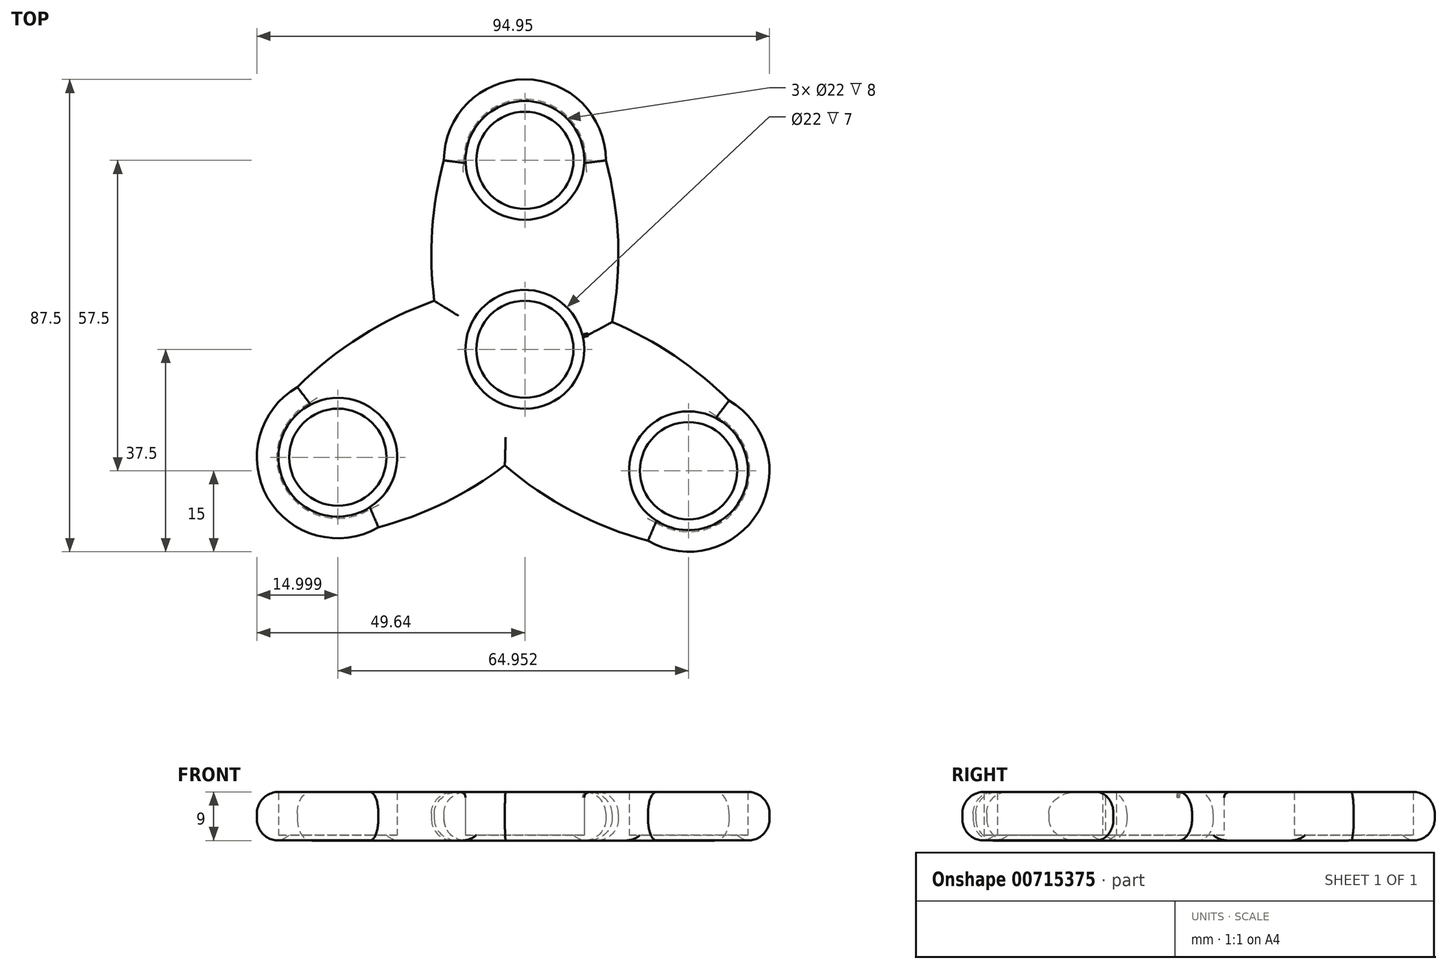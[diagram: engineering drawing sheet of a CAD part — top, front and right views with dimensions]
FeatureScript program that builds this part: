
annotation { "Feature Type Name" : "Feature", "Feature Type Description" : "" }
export const myFeature = defineFeature(function(context is Context, id is Id, definition is map)
    precondition{}
    {
        {
            var Q0;
            Q0=qCreatedBy(makeId("Top.planeOp"),FACE);
            var sketch = newSketch(context, id + "F0", { "sketchPlane" : qUnion([Q0])});
            skCircle(sketch, "E0", {"center": v(0, 0) * mm, "radius": 11 * mm});
            skPoint(sketch, "E1", {"position": v(11, 0) * mm});
            skPoint(sketch, "E2", {"position": v(-11, 0) * mm});
            skLineSegment(sketch, "E3", {"start": v(0, 0) * mm, "end": v(0, 35) * mm});
            skCircle(sketch, "E4", {"center": v(0, 0) * mm, "radius": 15 * mm});
            skCircle(sketch, "E5", {"center": v(0, 35) * mm, "radius": 11 * mm});
            skPoint(sketch, "E6", {"position": v(0, 46) * mm});
            skPoint(sketch, "E7", {"position": v(0, 24) * mm});
            skCircle(sketch, "E8", {"center": v(0, 35) * mm, "radius": 15 * mm});
            skArc(sketch, "E9", {"start": v(-15, 35) * mm, "mid": v(-17.31, 17.5) * mm, "end": v(-15, 0) * mm});
            skPoint(sketch, "E10.endSnap0", {"position": v(-17.31, 17.5) * mm});
            skPoint(sketch, "E11.MirrorP", {"position": v(17.31, 17.5) * mm});
            skArc(sketch, "E12.MirrorCS", {"start": v(15, 35) * mm, "mid": v(17.31, 17.5) * mm, "end": v(15, 0) * mm});
            skPoint(sketch, "E13.1.0", {"position": v(-10.83, -26.24) * mm});
            skCircle(sketch, "E13.1.1", {"center": v(-34.64, -20) * mm, "radius": 11 * mm});
            skPoint(sketch, "E13.1.2", {"position": v(-44.17, -25.5) * mm});
            skPoint(sketch, "E13.1.3", {"position": v(-25.11, -14.5) * mm});
            skPoint(sketch, "E13.1.4", {"position": v(-34.64, -20) * mm});
            skCircle(sketch, "E13.1.5", {"center": v(-34.64, -20) * mm, "radius": 15 * mm});
            skPoint(sketch, "E13.1.6", {"position": v(-28.14, 3.74) * mm});
            skPoint(sketch, "E13.1.7", {"position": v(-28.14, 3.74) * mm});
            skArc(sketch, "E13.1.8", {"start": v(-42.14, -7) * mm, "mid": v(-28.14, 3.74) * mm, "end": v(-11.83, 10.5) * mm});
            skArc(sketch, "E13.1.9", {"start": v(-27.14, -33) * mm, "mid": v(-10.83, -26.24) * mm, "end": v(3.17, -15.5) * mm});
            skPoint(sketch, "E13.2.0", {"position": v(23.81, 1.24) * mm});
            skCircle(sketch, "E13.2.1", {"center": v(30.31, -22.5) * mm, "radius": 11 * mm});
            skPoint(sketch, "E13.2.2", {"position": v(39.84, -28) * mm});
            skPoint(sketch, "E13.2.3", {"position": v(20.78, -17) * mm});
            skPoint(sketch, "E13.2.4", {"position": v(30.31, -22.5) * mm});
            skCircle(sketch, "E13.2.5", {"center": v(30.31, -22.5) * mm, "radius": 15 * mm});
            skPoint(sketch, "E13.2.6", {"position": v(6.5, -28.74) * mm});
            skPoint(sketch, "E13.2.7", {"position": v(6.5, -28.74) * mm});
            skArc(sketch, "E13.2.8", {"start": v(22.81, -35.5) * mm, "mid": v(6.5, -28.74) * mm, "end": v(-7.5, -18) * mm});
            skArc(sketch, "E13.2.9", {"start": v(37.81, -9.5) * mm, "mid": v(23.81, 1.24) * mm, "end": v(7.5, 8) * mm});
            skPoint(sketch, "E13.center", {"position": v(-1.44, -2.5) * mm});
            skCircle(sketch, "E14", {"center": v(0, 0) * mm, "radius": 9 * mm});
            skCircle(sketch, "E15", {"center": v(0, 35) * mm, "radius": 9 * mm});
            skCircle(sketch, "E16", {"center": v(30.31, -22.5) * mm, "radius": 9 * mm});
            skCircle(sketch, "E17", {"center": v(-34.64, -20) * mm, "radius": 9 * mm});
            skSolve(sketch);
        }
        {
            var Q0;
            Q0=makeQuery(id+"F0.imprint","IMPRINT",FACE,{"disambiguationData":[TD([[makeQuery(id+"F0.imprint","IMPRINT",EDGE,{"derivedFrom":sQuery(id+"F0.wireOp",EDGE,"E5")}),-1.0]])]});
            var Q1;
            {var subQ5=sQuery(id+"F0.wireOp",EDGE,"E3");var subQ7=sQuery(id+"F0.wireOp",EDGE,"E4");var subQ9=makeQuery(id+"F0.imprint","INTERSECT",VERTEX,{"derivedFrom":[subQ5,subQ7]});Q1=makeQuery(id+"F0.imprint","IMPRINT",FACE,{"disambiguationData":[TD([[makeQuery(id+"F0.imprint","IMPRINT",EDGE,{"disambiguationData":[TD([[subQ9,-1.0]])],"derivedFrom":subQ5}),1.0]])]});}
            var Q2;
            {var subQ5=sQuery(id+"F0.wireOp",EDGE,"E4");var subQ7=sQuery(id+"F0.wireOp",EDGE,"E3");var subQ8=makeQuery(id+"F0.imprint","INTERSECT",VERTEX,{"derivedFrom":[subQ7,subQ5]});Q2=makeQuery(id+"F0.imprint","IMPRINT",FACE,{"disambiguationData":[TD([[makeQuery(id+"F0.imprint","IMPRINT",EDGE,{"disambiguationData":[TD([[subQ8,-1.0]])],"derivedFrom":subQ7}),-1.0]])]});}
            var Q3;
            Q3=makeQuery(id+"F0.imprint","IMPRINT",FACE,{"disambiguationData":[TD([[makeQuery(id+"F0.imprint","IMPRINT",EDGE,{"derivedFrom":sQuery(id+"F0.wireOp",EDGE,"E0")}),-1.0]])]});
            var Q4;
            {var subQ3=sQuery(id+"F0.wireOp",EDGE,"E9");var subQ7=sQuery(id+"F0.wireOp",EDGE,"E4");var subQ8=makeQuery(id+"F0.imprint","INTERSECT",VERTEX,{"derivedFrom":[subQ7,subQ3]});Q4=makeQuery(id+"F0.imprint","IMPRINT",FACE,{"disambiguationData":[TD([[makeQuery(id+"F0.imprint","IMPRINT",EDGE,{"disambiguationData":[TD([[subQ8,-1.0]])],"derivedFrom":subQ7}),-1.0]])]});}
            var Q5;
            {var subQ0=sQuery(id+"F0.wireOp",EDGE,"E9");var subQ1=sQuery(id+"F0.wireOp",EDGE,"E4");var subQ2=makeQuery(id+"F0.imprint","INTERSECT",VERTEX,{"derivedFrom":[subQ1,subQ0]});Q5=makeQuery(id+"F0.imprint","IMPRINT",FACE,{"disambiguationData":[TD([[makeQuery(id+"F0.imprint","IMPRINT",EDGE,{"disambiguationData":[TD([[subQ2,1.0]])],"derivedFrom":subQ1}),-1.0]])]});}
            var Q6;
            Q6=makeQuery(id+"F0.imprint","IMPRINT",FACE,{"disambiguationData":[TD([[makeQuery(id+"F0.imprint","IMPRINT",EDGE,{"derivedFrom":sQuery(id+"F0.wireOp",EDGE,"E13.1.1")}),-1.0]])]});
            var Q7;
            {var subQ5=sQuery(id+"F0.wireOp",EDGE,"E12.MirrorCS");var subQ6=sQuery(id+"F0.wireOp",EDGE,"E4");var subQ7=makeQuery(id+"F0.imprint","INTERSECT",VERTEX,{"derivedFrom":[subQ6,subQ5]});Q7=makeQuery(id+"F0.imprint","IMPRINT",FACE,{"disambiguationData":[TD([[makeQuery(id+"F0.imprint","IMPRINT",EDGE,{"disambiguationData":[TD([[subQ7,1.0]])],"derivedFrom":subQ6}),-1.0]])]});}
            var Q8;
            {var subQ0=sQuery(id+"F0.wireOp",EDGE,"E13.1.9");var subQ1=sQuery(id+"F0.wireOp",EDGE,"E4");var subQ2=makeQuery(id+"F0.imprint","INTERSECT",VERTEX,{"derivedFrom":[subQ1,subQ0]});Q8=makeQuery(id+"F0.imprint","IMPRINT",FACE,{"disambiguationData":[TD([[makeQuery(id+"F0.imprint","IMPRINT",EDGE,{"disambiguationData":[TD([[subQ2,1.0]])],"derivedFrom":subQ1}),-1.0]])]});}
            var Q9;
            {var subQ0=sQuery(id+"F0.wireOp",EDGE,"E12.MirrorCS");var subQ1=sQuery(id+"F0.wireOp",EDGE,"E4");var subQ2=makeQuery(id+"F0.imprint","INTERSECT",VERTEX,{"derivedFrom":[subQ1,subQ0]});Q9=makeQuery(id+"F0.imprint","IMPRINT",FACE,{"disambiguationData":[TD([[makeQuery(id+"F0.imprint","IMPRINT",EDGE,{"disambiguationData":[TD([[subQ2,-1.0]])],"derivedFrom":subQ1}),-1.0]])]});}
            var Q10;
            Q10=makeQuery(id+"F0.imprint","IMPRINT",FACE,{"disambiguationData":[TD([[makeQuery(id+"F0.imprint","IMPRINT",EDGE,{"derivedFrom":sQuery(id+"F0.wireOp",EDGE,"E13.2.1")}),-1.0]])]});
            var Q11;
            {var subQ4=sQuery(id+"F0.wireOp",EDGE,"E3");var subQ5=sQuery(id+"F0.wireOp",EDGE,"E0");var subQ6=makeQuery(id+"F0.imprint","INTERSECT",VERTEX,{"derivedFrom":[subQ5,subQ4]});Q11=makeQuery(id+"F0.imprint","IMPRINT",FACE,{"disambiguationData":[TD([[makeQuery(id+"F0.imprint","IMPRINT",EDGE,{"disambiguationData":[TD([[subQ6,-1.0]])],"derivedFrom":subQ5}),-1.0]])]});}
            extrude(context, id + "F1", {"entities" : qUnion([Q0, Q1, Q2, Q3, Q4, Q5, Q6, Q7, Q8, Q9, Q10, Q11]), "depth" : 9 * mm, "offsetDistance" : 25 * mm});
        }
        {
            var Q0;
            Q0=makeQuery(id+"F0.imprint","IMPRINT",FACE,{"disambiguationData":[TD([[makeQuery(id+"F0.imprint","IMPRINT",EDGE,{"derivedFrom":sQuery(id+"F0.wireOp",EDGE,"E13.1.1")}),1.0]])]});
            var Q1;
            Q1=makeQuery(id+"F0.imprint","IMPRINT",FACE,{"disambiguationData":[TD([[makeQuery(id+"F0.imprint","IMPRINT",EDGE,{"derivedFrom":sQuery(id+"F0.wireOp",EDGE,"E0")}),1.0]])]});
            var Q2;
            Q2=makeQuery(id+"F0.imprint","IMPRINT",FACE,{"disambiguationData":[TD([[makeQuery(id+"F0.imprint","IMPRINT",EDGE,{"derivedFrom":sQuery(id+"F0.wireOp",EDGE,"E5")}),1.0]])]});
            var Q3;
            Q3=makeQuery(id+"F0.imprint","IMPRINT",FACE,{"disambiguationData":[TD([[makeQuery(id+"F0.imprint","IMPRINT",EDGE,{"derivedFrom":sQuery(id+"F0.wireOp",EDGE,"E13.2.1")}),1.0]])]});
            extrude(context, id + "F2", {"entities" : qUnion([Q0, Q1, Q2, Q3]), "operationType" : NewBodyOperationType.ADD, "depth" : 1 * mm, "offsetDistance" : 25 * mm});
        }
        {
            var Q0;
            Q0=makeQuery(id+"F1.opExtrude","CAP_EDGE",EDGE,{"disambiguationData":[OSD([sQuery(id+"F0.wireOp",EDGE,"E13.1.8")])],"isStart":false});
            var Q1;
            Q1=makeQuery(id+"F1.opExtrude","CAP_EDGE",EDGE,{"disambiguationData":[OSD([sQuery(id+"F0.wireOp",EDGE,"E13.1.5")])],"isStart":false});
            var Q2;
            Q2=makeQuery(id+"F1.opExtrude","CAP_EDGE",EDGE,{"disambiguationData":[OSD([sQuery(id+"F0.wireOp",EDGE,"E13.1.9")])],"isStart":false});
            var Q3;
            Q3=makeQuery(id+"F1.opExtrude","CAP_EDGE",EDGE,{"disambiguationData":[OSD([sQuery(id+"F0.wireOp",EDGE,"E8")])],"isStart":false});
            var Q4;
            Q4=makeQuery(id+"F1.opExtrude","CAP_EDGE",EDGE,{"disambiguationData":[OSD([sQuery(id+"F0.wireOp",EDGE,"E12.MirrorCS")])],"isStart":false});
            var Q5;
            Q5=makeQuery(id+"F1.opExtrude","CAP_EDGE",EDGE,{"disambiguationData":[OSD([sQuery(id+"F0.wireOp",EDGE,"E9")])],"isStart":false});
            var Q6;
            Q6=makeQuery(id+"F1.opExtrude","CAP_EDGE",EDGE,{"disambiguationData":[OSD([sQuery(id+"F0.wireOp",EDGE,"E13.2.9")])],"isStart":false});
            var Q7;
            Q7=makeQuery(id+"F1.opExtrude","CAP_EDGE",EDGE,{"disambiguationData":[OSD([sQuery(id+"F0.wireOp",EDGE,"E13.2.8")])],"isStart":false});
            var Q8;
            Q8=makeQuery(id+"F1.opExtrude","CAP_EDGE",EDGE,{"disambiguationData":[OSD([sQuery(id+"F0.wireOp",EDGE,"E13.2.5")])],"isStart":false});
            fillet(context, id + "F3", {"entities" : qUnion([Q0, Q1, Q2, Q3, Q4, Q5, Q6, Q7, Q8]), "radius" : 4 * mm, "tangentPropagation" : true, "allowEdgeOverflow" : false});
        }
        {
            var Q0;
            {var subQ0=sQuery(id+"F0.wireOp",EDGE,"E13.2.1");var subQ1=sQuery(id+"F0.wireOp",EDGE,"E13.1.1");var subQ2=sQuery(id+"F0.wireOp",EDGE,"E5");var subQ3=sQuery(id+"F0.wireOp",EDGE,"E0");Q0=makeQuery(id+"F2.boolean.opBoolean","MERGE",FACE,{"derivedFrom":[makeQuery(id+"F1.opExtrude","CAP_FACE",FACE,{"disambiguationData":[OSD([subQ3,subQ2,sQuery(id+"F0.wireOp",EDGE,"E8"),sQuery(id+"F0.wireOp",EDGE,"E9"),sQuery(id+"F0.wireOp",EDGE,"E12.MirrorCS"),subQ1,sQuery(id+"F0.wireOp",EDGE,"E13.1.5"),sQuery(id+"F0.wireOp",EDGE,"E13.1.8"),sQuery(id+"F0.wireOp",EDGE,"E13.1.9"),subQ0,sQuery(id+"F0.wireOp",EDGE,"E13.2.5"),sQuery(id+"F0.wireOp",EDGE,"E13.2.8"),sQuery(id+"F0.wireOp",EDGE,"E13.2.9")])],"isStart":true}),makeQuery(id+"F2.opExtrude","CAP_FACE",FACE,{"disambiguationData":[OSD([subQ3])],"isStart":true}),makeQuery(id+"F2.opExtrude","CAP_FACE",FACE,{"disambiguationData":[OSD([subQ2])],"isStart":true}),makeQuery(id+"F2.opExtrude","CAP_FACE",FACE,{"disambiguationData":[OSD([subQ1])],"isStart":true}),makeQuery(id+"F2.opExtrude","CAP_FACE",FACE,{"disambiguationData":[OSD([subQ0])],"isStart":true})]});}
            fillet(context, id + "F4", {"entities" : qUnion([Q0]), "radius" : 4 * mm, "tangentPropagation" : true, "allowEdgeOverflow" : false});
        }
        {
            var Q0;
            Q0=makeQuery(id+"F1.opExtrude","CAP_EDGE",EDGE,{"disambiguationData":[OSD([sQuery(id+"F0.wireOp",EDGE,"E0")])],"isStart":false});
            fillet(context, id + "F5", {"entities" : qUnion([Q0]), "radius" : 1 * mm, "tangentPropagation" : true, "allowEdgeOverflow" : false});
        }
    });
